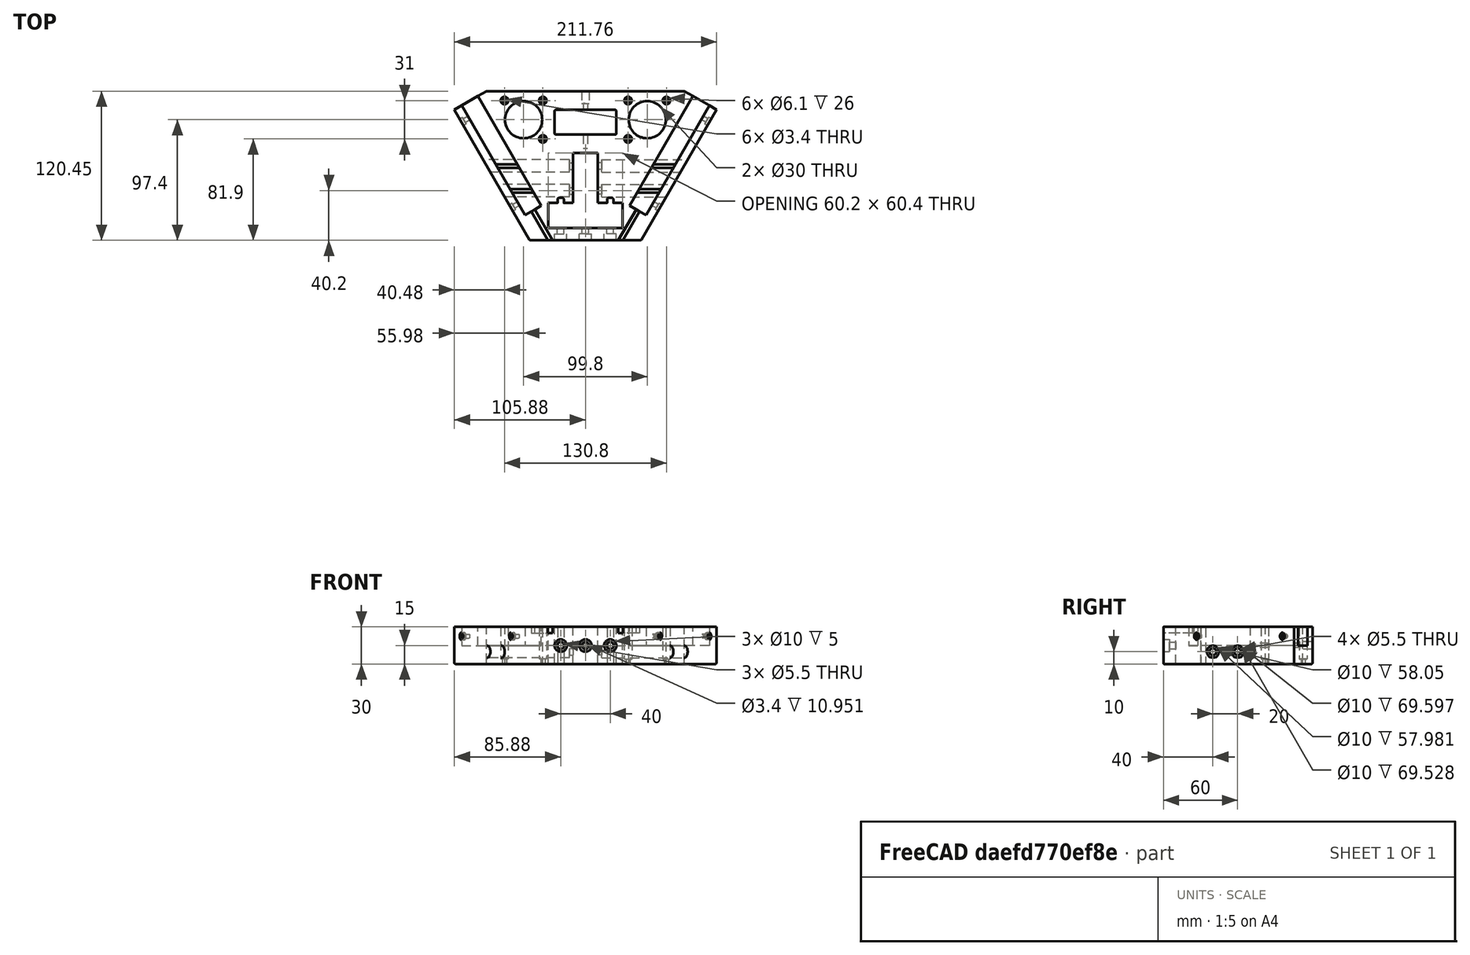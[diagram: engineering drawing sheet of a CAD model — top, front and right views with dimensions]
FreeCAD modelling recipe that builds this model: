
FCSTD DOCUMENT  (FreeCAD 2022.430R26244 +4758 (Git))
Label: As3TopCorner
License: All rights reserved
LicenseURL: http://en.wikipedia.org/wiki/All_rights_reserved
objects: Part::FeaturePython×12, App::FeaturePython×2, Part::Feature×1
note: 12 computed .brp shape members not serialized (recipe doc carries the construction recipe); baked Part::Feature solids carry a one-line shape summary decoded from their .brp

FEATURE [App::FeaturePython] Constraints  # WARN: FeaturePython — macro-defined, semantics opaque (R4)
  TreeRank = 0
  _LinkVersion = 1
  _Version = 1
FEATURE [Part::Feature] ShapeCopy  label="TopCorner"
  Placement = pos=(-1.75e-14,-0.999998,-2.49e-14) rot=(0,0,1;0rad)
  TreeRank = 6
  shape: bbox 211.8 x 120.4 x 30 mm, 156 faces (baked)
FEATURE [Part::FeaturePython] Parts  # WARN: FeaturePython — macro-defined, semantics opaque (R4)
  Group = -> [ShapeCopy]
  GroupMode = 0
  TreeRank = 0
  _LinkVersion = 1
FEATURE [Part::FeaturePython] Assembly  label="As3TopCorner"  # WARN: FeaturePython — macro-defined, semantics opaque (R4)
  AutoRelax = true
  BuildShape = 0
  Freeze = false
  Group = -> [Constraints,Elements,Parts]
  TreeRank = 0
  Verbose = false
  _LinkVersion = 1
  _SolverType = 1
  _Version = 1
FEATURE [App::FeaturePython] Elements  # WARN: FeaturePython — macro-defined, semantics opaque (R4)
  Group = -> [Element,Element001,Element002,Element004,Element005,Element006,Element007,Element008,Element009,Element010]
  TreeRank = 0
  _LinkVersion = 1
FEATURE [Part::FeaturePython] Element  label="FaceHsup"  # link proxy (typed FeaturePython)
  Detach = false
  LinkTransform = true
  LinkedObject = -> ShapeCopy [Face23]
  TreeRank = 0
  _LinkVersion = 1
  _Parent = -> Elements
FEATURE [Part::FeaturePython] Element001  label="AppuiPoteau1"  # link proxy (typed FeaturePython)
  Detach = false
  LinkTransform = true
  LinkedObject = -> ShapeCopy [Face46]
  TreeRank = 0
  _LinkVersion = 1
  _Parent = -> Elements
FEATURE [Part::FeaturePython] Element002  label="AppuiPoteau2"  # link proxy (typed FeaturePython)
  Detach = false
  LinkTransform = true
  LinkedObject = -> ShapeCopy [Face44]
  TreeRank = 0
  _LinkVersion = 1
  _Parent = -> Elements
FEATURE [Part::FeaturePython] Element004  label="AppuiTravExtr1"  # link proxy (typed FeaturePython)
  Detach = false
  LinkTransform = true
  LinkedObject = -> ShapeCopy [Face18]
  TreeRank = 0
  _LinkVersion = 1
  _Parent = -> Elements
FEATURE [Part::FeaturePython] Element005  label="AppuiTrav1h"  # link proxy (typed FeaturePython)
  Detach = false
  LinkTransform = true
  LinkedObject = -> ShapeCopy [Face77]
  TreeRank = 0
  _LinkVersion = 1
  _Parent = -> Elements
FEATURE [Part::FeaturePython] Element006  label="AppuiTravExtr2"  # link proxy (typed FeaturePython)
  Detach = false
  LinkTransform = true
  LinkedObject = -> ShapeCopy [Face25]
  TreeRank = 0
  _LinkVersion = 1
  _Parent = -> Elements
FEATURE [Part::FeaturePython] Element007  label="AppuiTrav1v"  # link proxy (typed FeaturePython)
  Detach = false
  LinkTransform = true
  LinkedObject = -> ShapeCopy [Face27]
  TreeRank = 0
  _LinkVersion = 1
  _Parent = -> Elements
FEATURE [Part::FeaturePython] Element008  label="AppuiTrav2v"  # link proxy (typed FeaturePython)
  Detach = false
  LinkTransform = true
  LinkedObject = -> ShapeCopy [Face20]
  TreeRank = 0
  _LinkVersion = 1
  _Parent = -> Elements
FEATURE [Part::FeaturePython] Element009  label="AppuiLatPoteau21"  # link proxy (typed FeaturePython)
  Detach = false
  LinkTransform = true
  LinkedObject = -> ShapeCopy [Face33]
  TreeRank = 0
  _LinkVersion = 1
  _Parent = -> Elements
FEATURE [Part::FeaturePython] Element010  label="AppuiLatPoteau22"  # link proxy (typed FeaturePython)
  Detach = false
  LinkTransform = true
  LinkedObject = -> ShapeCopy [Face37]
  TreeRank = 0
  _LinkVersion = 1
  _Parent = -> Elements
